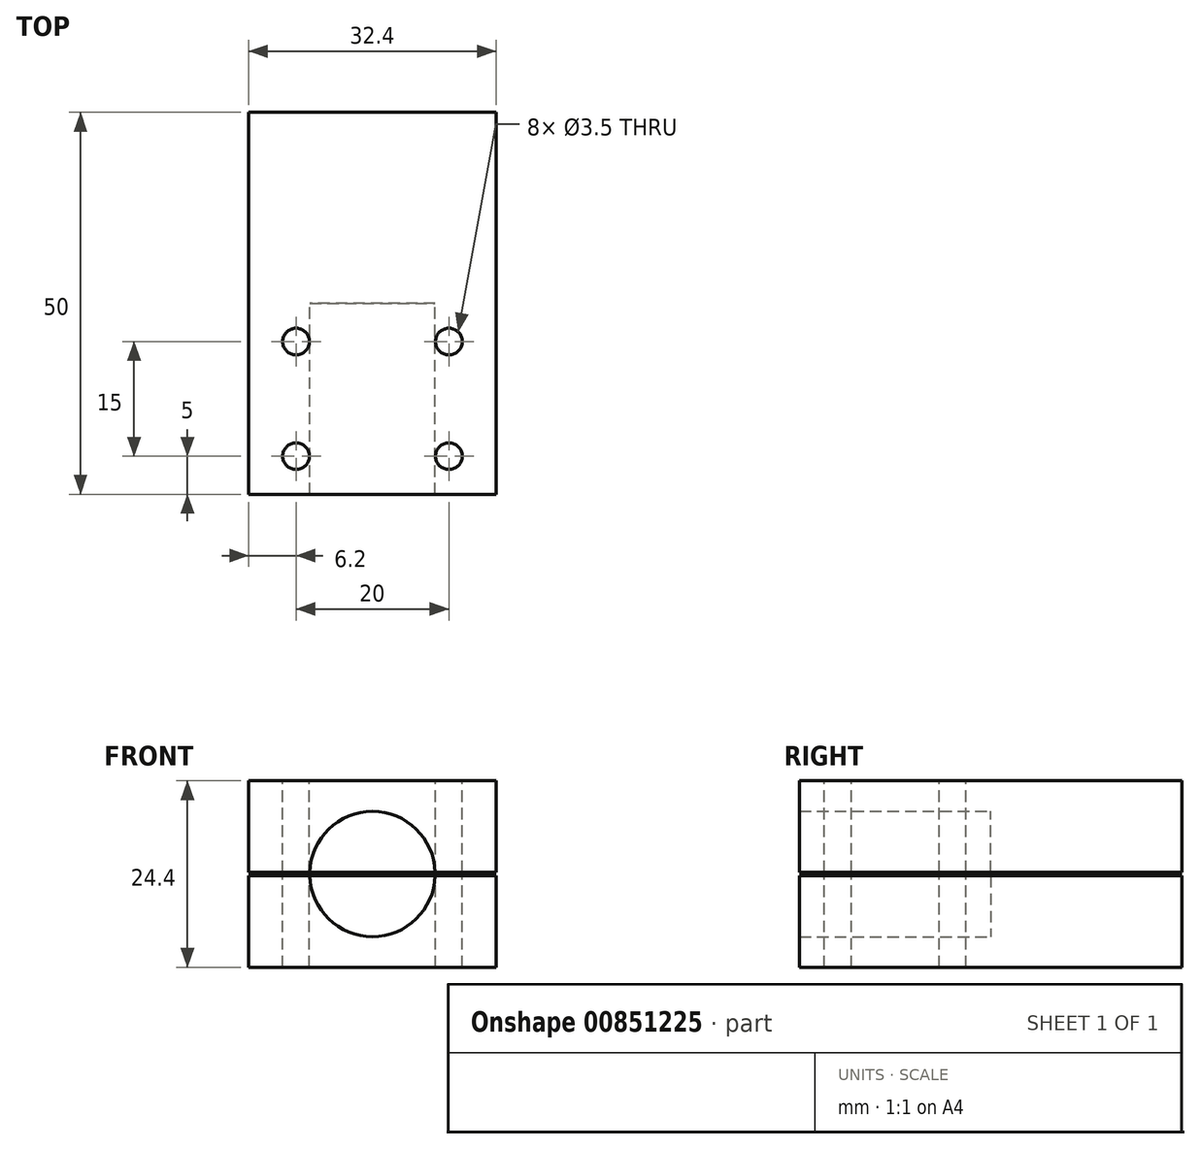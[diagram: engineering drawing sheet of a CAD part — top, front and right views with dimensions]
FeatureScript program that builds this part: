
annotation { "Feature Type Name" : "Feature", "Feature Type Description" : "" }
export const myFeature = defineFeature(function(context is Context, id is Id, definition is map)
    precondition{}
    {
        {
            var Q0;
            Q0=qCreatedBy(makeId("Front.planeOp"),FACE);
            var sketch = newSketch(context, id + "F0", { "sketchPlane" : qUnion([Q0])});
            skArc(sketch, "E0", {"start": v(-8.2, -0.25) * mm, "mid": v(0, -8.2) * mm, "end": v(8.2, -0.25) * mm});
            skLineSegment(sketch, "E1.bottom", {"start": v(16.2, -12.2) * mm, "end": v(-16.2, -12.2) * mm});
            skLineSegment(sketch, "E1.top", {"start": v(16.2, 12.2) * mm, "end": v(-16.2, 12.2) * mm});
            skLineSegment(sketch, "E1.left", {"start": v(16.2, -12.2) * mm, "end": v(16.2, -0.25) * mm});
            skLineSegment(sketch, "E1.right", {"start": v(-16.2, -12.2) * mm, "end": v(-16.2, -0.25) * mm});
            skLineSegment(sketch, "E2", {"start": v(-16.2, 0) * mm, "end": v(16.2, 0) * mm, "construction": true});
            skLineSegment(sketch, "E3.0", {"start": v(-16.2, -0.25) * mm, "end": v(-8.2, -0.25) * mm});
            skLineSegment(sketch, "E4.0", {"start": v(-16.2, 0.25) * mm, "end": v(-8.2, 0.25) * mm});
            skLineSegment(sketch, "E5.trimOffspring", {"start": v(16.2, 0.25) * mm, "end": v(16.2, 12.2) * mm});
            skLineSegment(sketch, "E6.trimOffspring", {"start": v(-16.2, 0.25) * mm, "end": v(-16.2, 12.2) * mm});
            skArc(sketch, "E7.trimOffspring", {"start": v(8.2, 0.25) * mm, "mid": v(0, 8.2) * mm, "end": v(-8.2, 0.25) * mm});
            skLineSegment(sketch, "E8.trimOffspring", {"start": v(8.2, -0.25) * mm, "end": v(16.2, -0.25) * mm});
            skLineSegment(sketch, "E9.trimOffspring", {"start": v(8.2, 0.25) * mm, "end": v(16.2, 0.25) * mm});
            skSolve(sketch);
        }
        {
            var Q0;
            Q0 = qSketchRegion(id + "F0", true);
            extrude(context, id + "F1", {"entities" : qUnion([Q0]), "depth" : 25 * mm, "offsetDistance" : 25 * mm});
        }
        {
            var Q0;
            Q0=makeQuery(id+"F1.opExtrude","CAP_FACE",FACE,{"disambiguationData":[OSD([sQuery(id+"F0.wireOp",EDGE,"E1.top"),sQuery(id+"F0.wireOp",EDGE,"E4.0"),sQuery(id+"F0.wireOp",EDGE,"E5.trimOffspring"),sQuery(id+"F0.wireOp",EDGE,"E6.trimOffspring"),sQuery(id+"F0.wireOp",EDGE,"E7.trimOffspring"),sQuery(id+"F0.wireOp",EDGE,"E9.trimOffspring")])],"isStart":true});
            var sketch = newSketch(context, id + "F2", { "sketchPlane" : qUnion([Q0])});
            skLineSegment(sketch, "E10.bottom", {"start": v(-16.2, 12.2) * mm, "end": v(16.2, 12.2) * mm});
            skLineSegment(sketch, "E10.top", {"start": v(-16.2, 0.25) * mm, "end": v(16.2, 0.25) * mm});
            skLineSegment(sketch, "E10.left", {"start": v(-16.2, 12.2) * mm, "end": v(-16.2, 0.25) * mm});
            skLineSegment(sketch, "E10.right", {"start": v(16.2, 12.2) * mm, "end": v(16.2, 0.25) * mm});
            skSolve(sketch);
        }
        {
            var Q0;
            Q0 = qSketchRegion(id + "F2", true);
            extrude(context, id + "F3", {"entities" : qUnion([Q0]), "operationType" : NewBodyOperationType.ADD, "depth" : 25 * mm, "offsetDistance" : 25 * mm});
        }
        {
            var Q0;
            Q0=makeQuery(id+"F1.opExtrude","CAP_FACE",FACE,{"disambiguationData":[OSD([sQuery(id+"F0.wireOp",EDGE,"E0"),sQuery(id+"F0.wireOp",EDGE,"E1.bottom"),sQuery(id+"F0.wireOp",EDGE,"E1.left"),sQuery(id+"F0.wireOp",EDGE,"E1.right"),sQuery(id+"F0.wireOp",EDGE,"E3.0"),sQuery(id+"F0.wireOp",EDGE,"E8.trimOffspring")])],"isStart":true});
            var sketch = newSketch(context, id + "F4", { "sketchPlane" : qUnion([Q0])});
            skLineSegment(sketch, "E11.bottom", {"start": v(-16.2, -0.25) * mm, "end": v(16.2, -0.25) * mm});
            skLineSegment(sketch, "E11.top", {"start": v(-16.2, -12.2) * mm, "end": v(16.2, -12.2) * mm});
            skLineSegment(sketch, "E11.left", {"start": v(-16.2, -0.25) * mm, "end": v(-16.2, -12.2) * mm});
            skLineSegment(sketch, "E11.right", {"start": v(16.2, -0.25) * mm, "end": v(16.2, -12.2) * mm});
            skSolve(sketch);
        }
        {
            var Q0;
            Q0 = qSketchRegion(id + "F4", true);
            extrude(context, id + "F5", {"entities" : qUnion([Q0]), "operationType" : NewBodyOperationType.ADD, "depth" : 25 * mm, "offsetDistance" : 25 * mm});
        }
        {
            var Q0;
            Q0=makeQuery(id+"F3.boolean.opBoolean","MERGE",FACE,{"derivedFrom":[makeQuery(id+"F1.opExtrude","SWEPT_FACE",FACE,{"disambiguationData":[OSD([sQuery(id+"F0.wireOp",EDGE,"E1.top")])]}),makeQuery(id+"F3.opExtrude","SWEPT_FACE",FACE,{"disambiguationData":[OSD([sQuery(id+"F2.wireOp",EDGE,"E10.bottom")])]})]});
            var sketch = newSketch(context, id + "F6", { "sketchPlane" : qUnion([Q0])});
            skLineSegment(sketch, "E12.bottom", {"start": v(-10, -20) * mm, "end": v(10, -20) * mm, "construction": true});
            skLineSegment(sketch, "E12.top", {"start": v(-10, -5) * mm, "end": v(10, -5) * mm, "construction": true});
            skLineSegment(sketch, "E12.left", {"start": v(-10, -20) * mm, "end": v(-10, -5) * mm, "construction": true});
            skLineSegment(sketch, "E12.right", {"start": v(10, -20) * mm, "end": v(10, -5) * mm, "construction": true});
            skCircle(sketch, "E13", {"center": v(10, -5) * mm, "radius": 1.75 * mm});
            skCircle(sketch, "E14", {"center": v(-10, -5) * mm, "radius": 1.75 * mm});
            skCircle(sketch, "E15", {"center": v(-10, -20) * mm, "radius": 1.75 * mm});
            skCircle(sketch, "E16", {"center": v(10, -20) * mm, "radius": 1.75 * mm});
            skLineSegment(sketch, "E17", {"start": v(0, -25) * mm, "end": v(0, -20) * mm, "construction": true});
            skSolve(sketch);
        }
        {
            var Q0;
            Q0 = qSketchRegion(id + "F6", true);
            var Q1;
            Q1=makeQuery(id+"F5.boolean.opBoolean","MERGE",FACE,{"derivedFrom":[makeQuery(id+"F1.opExtrude","SWEPT_FACE",FACE,{"disambiguationData":[OSD([sQuery(id+"F0.wireOp",EDGE,"E1.bottom")])]}),makeQuery(id+"F5.opExtrude","SWEPT_FACE",FACE,{"disambiguationData":[OSD([sQuery(id+"F4.wireOp",EDGE,"E11.top")])]})]});
            extrude(context, id + "F7", {"entities" : qUnion([Q0]), "operationType" : NewBodyOperationType.REMOVE, "endBound" : BoundingType.UP_TO_SURFACE, "oppositeDirection" : true, "depth" : 25 * mm, "endBoundEntityFace" : qUnion([Q1]), "offsetDistance" : 25 * mm});
        }
    });
